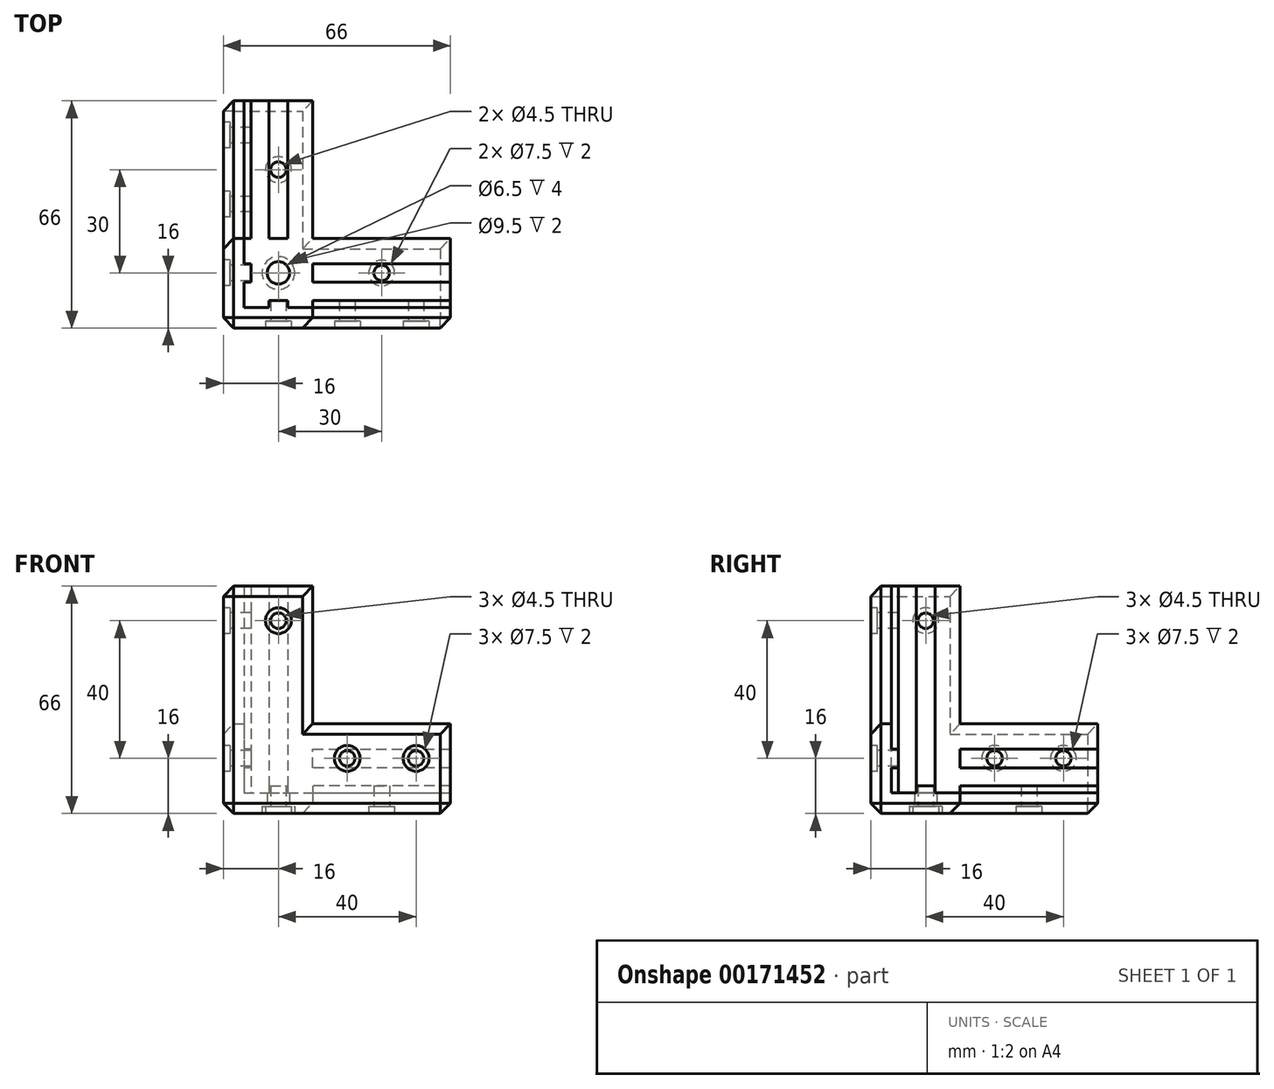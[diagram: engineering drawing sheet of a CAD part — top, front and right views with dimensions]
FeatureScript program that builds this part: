
annotation { "Feature Type Name" : "Feature", "Feature Type Description" : "" }
export const myFeature = defineFeature(function(context is Context, id is Id, definition is map)
    precondition{}
    {
        {
            var Q0;
            Q0=qCreatedBy(makeId("Top.planeOp"),FACE);
            var sketch = newSketch(context, id + "F0", { "sketchPlane" : qUnion([Q0])});
            skLineSegment(sketch, "E0", {"start": v(0, 0) * mm, "end": v(0, 66) * mm});
            skLineSegment(sketch, "E1", {"start": v(0, 66) * mm, "end": v(26, 66) * mm});
            skLineSegment(sketch, "E2", {"start": v(26, 66) * mm, "end": v(26, 26) * mm});
            skLineSegment(sketch, "E3", {"start": v(26, 26) * mm, "end": v(66, 26) * mm});
            skLineSegment(sketch, "E4", {"start": v(66, 26) * mm, "end": v(66, 0) * mm});
            skLineSegment(sketch, "E5", {"start": v(66, 0) * mm, "end": v(0, 0) * mm});
            skLineSegment(sketch, "E6", {"start": v(66, 6) * mm, "end": v(6, 6) * mm, "construction": true});
            skLineSegment(sketch, "E7", {"start": v(6, 6) * mm, "end": v(6, 66) * mm, "construction": true});
            skSolve(sketch);
        }
        {
            var Q0;
            Q0=qSketchRegion(id+"F0",true);
            extrude(context, id + "F1", {"entities" : qUnion([Q0]), "depth" : 6 * mm});
        }
        {
            var Q0;
            Q0=makeQuery(id+"F1.opExtrude","CAP_FACE",FACE,{"disambiguationData":[OSD([sQuery(id+"F0.wireOp",EDGE,"E0"),sQuery(id+"F0.wireOp",EDGE,"E1"),sQuery(id+"F0.wireOp",EDGE,"E2"),sQuery(id+"F0.wireOp",EDGE,"E3"),sQuery(id+"F0.wireOp",EDGE,"E4"),sQuery(id+"F0.wireOp",EDGE,"E5")])],"isStart":false});
            var sketch = newSketch(context, id + "F2", { "sketchPlane" : qUnion([Q0])});
            skLineSegment(sketch, "E8", {"start": v(0, 66) * mm, "end": v(6, 66) * mm});
            skLineSegment(sketch, "E9", {"start": v(6, 66) * mm, "end": v(6, 6) * mm});
            skLineSegment(sketch, "E10", {"start": v(6, 6) * mm, "end": v(66, 6) * mm});
            skLineSegment(sketch, "E11", {"start": v(66, 6) * mm, "end": v(66, 0) * mm});
            skLineSegment(sketch, "E12", {"start": v(66, 0) * mm, "end": v(0, 0) * mm});
            skLineSegment(sketch, "E13", {"start": v(0, 0) * mm, "end": v(0, 66) * mm});
            skSolve(sketch);
        }
        {
            var Q0;
            Q0=makeQuery(id+"F2.imprint","IMPRINT",FACE,{"disambiguationData":[TD([[makeQuery(id+"F2.imprint","IMPRINT",EDGE,{"derivedFrom":sQuery(id+"F2.wireOp",EDGE,"E8")}),-1.0]])]});
            extrude(context, id + "F3", {"entities" : qUnion([Q0]), "operationType" : NewBodyOperationType.ADD, "depth" : 20 * mm});
        }
        {
            var Q0;
            Q0=makeQuery(id+"F3.opExtrude","CAP_FACE",FACE,{"disambiguationData":[OSD([sQuery(id+"F2.wireOp",EDGE,"E8"),sQuery(id+"F2.wireOp",EDGE,"E9"),sQuery(id+"F2.wireOp",EDGE,"E10"),sQuery(id+"F2.wireOp",EDGE,"E11"),sQuery(id+"F2.wireOp",EDGE,"E12"),sQuery(id+"F2.wireOp",EDGE,"E13")])],"isStart":false});
            var sketch = newSketch(context, id + "F4", { "sketchPlane" : qUnion([Q0])});
            skLineSegment(sketch, "E14", {"start": v(6, 26) * mm, "end": v(0, 26) * mm});
            skLineSegment(sketch, "E15", {"start": v(0, 26) * mm, "end": v(0, 0) * mm});
            skLineSegment(sketch, "E16", {"start": v(0, 0) * mm, "end": v(26, 0) * mm});
            skLineSegment(sketch, "E17", {"start": v(26, 0) * mm, "end": v(26, 6) * mm});
            skLineSegment(sketch, "E18", {"start": v(26, 6) * mm, "end": v(6, 6) * mm});
            skLineSegment(sketch, "E19", {"start": v(6, 6) * mm, "end": v(6, 26) * mm});
            skSolve(sketch);
        }
        {
            var Q0;
            Q0=qSketchRegion(id+"F4",true);
            extrude(context, id + "F5", {"entities" : qUnion([Q0]), "operationType" : NewBodyOperationType.ADD, "depth" : 40 * mm});
        }
        {
            var Q0;
            Q0=makeQuery(id+"F1.opExtrude","CAP_FACE",FACE,{"disambiguationData":[OSD([sQuery(id+"F0.wireOp",EDGE,"E0"),sQuery(id+"F0.wireOp",EDGE,"E1"),sQuery(id+"F0.wireOp",EDGE,"E2"),sQuery(id+"F0.wireOp",EDGE,"E3"),sQuery(id+"F0.wireOp",EDGE,"E4"),sQuery(id+"F0.wireOp",EDGE,"E5")])],"isStart":false});
            var sketch = newSketch(context, id + "F6", { "sketchPlane" : qUnion([Q0])});
            skLineSegment(sketch, "E20", {"start": v(66, 16) * mm, "end": v(6, 16) * mm, "construction": true});
            skLineSegment(sketch, "E21", {"start": v(16, 66) * mm, "end": v(16, 6) * mm, "construction": true});
            skLineSegment(sketch, "E22", {"start": v(16, 6) * mm, "end": v(18.71, 6) * mm});
            skLineSegment(sketch, "E23", {"start": v(18.71, 6) * mm, "end": v(18.71, 8) * mm});
            skLineSegment(sketch, "E24", {"start": v(18.71, 8) * mm, "end": v(13.3, 8) * mm});
            skLineSegment(sketch, "E25", {"start": v(13.3, 8) * mm, "end": v(13.3, 6) * mm});
            skLineSegment(sketch, "E26", {"start": v(13.3, 6) * mm, "end": v(16, 6) * mm});
            skLineSegment(sketch, "E27", {"start": v(6, 16) * mm, "end": v(6, 18.7) * mm});
            skLineSegment(sketch, "E28", {"start": v(6, 18.7) * mm, "end": v(8, 18.7) * mm});
            skLineSegment(sketch, "E29", {"start": v(8, 18.7) * mm, "end": v(8, 13.29) * mm});
            skLineSegment(sketch, "E30", {"start": v(8, 13.29) * mm, "end": v(6, 13.29) * mm});
            skLineSegment(sketch, "E31", {"start": v(6, 13.29) * mm, "end": v(6, 16) * mm});
            skSolve(sketch);
        }
        {
            var Q0;
            Q0=qSketchRegion(id+"F6",true);
            extrude(context, id + "F7", {"entities" : qUnion([Q0]), "operationType" : NewBodyOperationType.ADD, "depth" : 60 * mm});
        }
        {
            var Q0;
            Q0=makeQuery(id+"F1.opExtrude","CAP_FACE",FACE,{"disambiguationData":[OSD([sQuery(id+"F0.wireOp",EDGE,"E0"),sQuery(id+"F0.wireOp",EDGE,"E1"),sQuery(id+"F0.wireOp",EDGE,"E2"),sQuery(id+"F0.wireOp",EDGE,"E3"),sQuery(id+"F0.wireOp",EDGE,"E4"),sQuery(id+"F0.wireOp",EDGE,"E5")])],"isStart":false});
            var sketch = newSketch(context, id + "F8", { "sketchPlane" : qUnion([Q0])});
            skLineSegment(sketch, "E32", {"start": v(66, 16) * mm, "end": v(8, 16) * mm, "construction": true});
            skLineSegment(sketch, "E33", {"start": v(66, 16) * mm, "end": v(66, 18.7) * mm});
            skLineSegment(sketch, "E34", {"start": v(66, 18.7) * mm, "end": v(26, 18.7) * mm});
            skLineSegment(sketch, "E35", {"start": v(26, 18.7) * mm, "end": v(26, 13.29) * mm});
            skLineSegment(sketch, "E36", {"start": v(26, 13.29) * mm, "end": v(66, 13.29) * mm});
            skLineSegment(sketch, "E37", {"start": v(66, 13.29) * mm, "end": v(66, 16) * mm});
            skLineSegment(sketch, "E38", {"start": v(16, 66) * mm, "end": v(16, 8) * mm, "construction": true});
            skLineSegment(sketch, "E39", {"start": v(16, 66) * mm, "end": v(13.3, 66) * mm});
            skLineSegment(sketch, "E40", {"start": v(13.3, 66) * mm, "end": v(13.3, 26) * mm});
            skLineSegment(sketch, "E41", {"start": v(13.3, 26) * mm, "end": v(18.7, 26) * mm});
            skLineSegment(sketch, "E42", {"start": v(18.7, 26) * mm, "end": v(18.7, 66) * mm});
            skLineSegment(sketch, "E43", {"start": v(18.7, 66) * mm, "end": v(16, 66) * mm});
            skSolve(sketch);
        }
        {
            var Q0;
            Q0=qSketchRegion(id+"F8",true);
            extrude(context, id + "F9", {"entities" : qUnion([Q0]), "operationType" : NewBodyOperationType.ADD, "depth" : 2 * mm});
        }
        {
            var Q0;
            {var subQ1=sQuery(id+"F2.wireOp",EDGE,"E10");var subQ2=sQuery(id+"F0.wireOp",EDGE,"E4");var subQ3=sQuery(id+"F4.wireOp",EDGE,"E18");Q0=makeQuery(id+"F7.boolean.opBoolean","SPLIT",FACE,{"disambiguationData":[TD([makeQuery(id+"F1.opExtrude","SWEPT_FACE",FACE,{"disambiguationData":[OSD([subQ2])]})])],"derivedFrom":makeQuery(id+"F5.boolean.opBoolean","MERGE",FACE,{"derivedFrom":[makeQuery(id+"F3.opExtrude","SWEPT_FACE",FACE,{"disambiguationData":[OSD([subQ1])]}),makeQuery(id+"F5.opExtrude","SWEPT_FACE",FACE,{"disambiguationData":[OSD([subQ3])]})]})});}
            var sketch = newSketch(context, id + "F10", { "sketchPlane" : qUnion([Q0])});
            skLineSegment(sketch, "E44", {"start": v(-66, 16) * mm, "end": v(-26, 16) * mm, "construction": true});
            skLineSegment(sketch, "E45", {"start": v(-66, 16) * mm, "end": v(-66, 13.3) * mm});
            skLineSegment(sketch, "E46", {"start": v(-66, 13.3) * mm, "end": v(-26, 13.3) * mm});
            skLineSegment(sketch, "E47", {"start": v(-26, 13.3) * mm, "end": v(-26, 16) * mm});
            skLineSegment(sketch, "E48", {"start": v(-26, 18.71) * mm, "end": v(-66, 18.71) * mm});
            skLineSegment(sketch, "E49", {"start": v(-66, 18.71) * mm, "end": v(-66, 16) * mm});
            skLineSegment(sketch, "E50", {"start": v(-26, 18.71) * mm, "end": v(-26, 16) * mm});
            skSolve(sketch);
        }
        {
            var Q0;
            Q0=qSketchRegion(id+"F10",true);
            extrude(context, id + "F11", {"entities" : qUnion([Q0]), "operationType" : NewBodyOperationType.ADD, "depth" : 2 * mm});
        }
        {
            var Q0;
            {var subQ0=sQuery(id+"F2.wireOp",EDGE,"E9");var subQ3=sQuery(id+"F0.wireOp",EDGE,"E1");var subQ5=sQuery(id+"F4.wireOp",EDGE,"E19");Q0=makeQuery(id+"F7.boolean.opBoolean","SPLIT",FACE,{"disambiguationData":[TD([makeQuery(id+"F1.opExtrude","SWEPT_FACE",FACE,{"disambiguationData":[OSD([subQ3])]})])],"derivedFrom":makeQuery(id+"F5.boolean.opBoolean","MERGE",FACE,{"derivedFrom":[makeQuery(id+"F3.opExtrude","SWEPT_FACE",FACE,{"disambiguationData":[OSD([subQ0])]}),makeQuery(id+"F5.opExtrude","SWEPT_FACE",FACE,{"disambiguationData":[OSD([subQ5])]})]})});}
            var sketch = newSketch(context, id + "F12", { "sketchPlane" : qUnion([Q0])});
            skLineSegment(sketch, "E51", {"start": v(66, 16) * mm, "end": v(26, 16) * mm, "construction": true});
            skLineSegment(sketch, "E52", {"start": v(66, 16) * mm, "end": v(66, 18.71) * mm});
            skLineSegment(sketch, "E53", {"start": v(66, 18.71) * mm, "end": v(26, 18.7) * mm});
            skLineSegment(sketch, "E54", {"start": v(26, 18.7) * mm, "end": v(26, 13.29) * mm});
            skLineSegment(sketch, "E55", {"start": v(26, 13.29) * mm, "end": v(66, 13.29) * mm});
            skLineSegment(sketch, "E56", {"start": v(66, 16) * mm, "end": v(66, 13.29) * mm});
            skSolve(sketch);
        }
        {
            var Q0;
            Q0=qSketchRegion(id+"F12",true);
            extrude(context, id + "F13", {"entities" : qUnion([Q0]), "operationType" : NewBodyOperationType.ADD, "depth" : 2 * mm});
        }
        {
            var Q0;
            Q0=makeQuery(id+"F5.boolean.opBoolean","MERGE",FACE,{"derivedFrom":[makeQuery(id+"F3.boolean.opBoolean","MERGE",FACE,{"derivedFrom":[makeQuery(id+"F1.opExtrude","SWEPT_FACE",FACE,{"disambiguationData":[OSD([sQuery(id+"F0.wireOp",EDGE,"E5")])]}),makeQuery(id+"F3.opExtrude","SWEPT_FACE",FACE,{"disambiguationData":[OSD([sQuery(id+"F2.wireOp",EDGE,"E12")])]})]}),makeQuery(id+"F5.opExtrude","SWEPT_FACE",FACE,{"disambiguationData":[OSD([sQuery(id+"F4.wireOp",EDGE,"E16")])]})]});
            var sketch = newSketch(context, id + "F14", { "sketchPlane" : qUnion([Q0])});
            skLineSegment(sketch, "E57", {"start": v(6, 66) * mm, "end": v(6, 6) * mm, "construction": true});
            skLineSegment(sketch, "E58", {"start": v(6, 6) * mm, "end": v(66, 6) * mm, "construction": true});
            skCircle(sketch, "E59", {"center": v(56, 16) * mm, "radius": 2.25 * mm});
            skCircle(sketch, "E60", {"center": v(36, 16) * mm, "radius": 2.25 * mm});
            skCircle(sketch, "E61", {"center": v(16, 56) * mm, "radius": 2.25 * mm});
            skLineSegment(sketch, "E62", {"start": v(26, 26) * mm, "end": v(6, 26) * mm, "construction": true});
            skLineSegment(sketch, "E63", {"start": v(26, 26) * mm, "end": v(26, 6) * mm, "construction": true});
            skSolve(sketch);
        }
        {
            var Q0;
            Q0=makeQuery(id+"F14.imprint","IMPRINT",FACE,{"disambiguationData":[TD([[makeQuery(id+"F14.imprint","IMPRINT",EDGE,{"derivedFrom":sQuery(id+"F14.wireOp",EDGE,"E59")}),1.0]])]});
            var Q1;
            Q1=makeQuery(id+"F14.imprint","IMPRINT",FACE,{"disambiguationData":[TD([[makeQuery(id+"F14.imprint","IMPRINT",EDGE,{"derivedFrom":sQuery(id+"F14.wireOp",EDGE,"E61")}),1.0]])]});
            var Q2;
            Q2=makeQuery(id+"F14.imprint","IMPRINT",FACE,{"disambiguationData":[TD([[makeQuery(id+"F14.imprint","IMPRINT",EDGE,{"derivedFrom":sQuery(id+"F14.wireOp",EDGE,"E60")}),1.0]])]});
            extrude(context, id + "F15", {"entities" : qUnion([Q0, Q1, Q2]), "operationType" : NewBodyOperationType.REMOVE, "endBound" : BoundingType.UP_TO_NEXT, "oppositeDirection" : true, "depth" : 25 * mm});
        }
        {
            var Q0;
            Q0=makeQuery(id+"F5.boolean.opBoolean","MERGE",FACE,{"derivedFrom":[makeQuery(id+"F3.boolean.opBoolean","MERGE",FACE,{"derivedFrom":[makeQuery(id+"F1.opExtrude","SWEPT_FACE",FACE,{"disambiguationData":[OSD([sQuery(id+"F0.wireOp",EDGE,"E0")])]}),makeQuery(id+"F3.opExtrude","SWEPT_FACE",FACE,{"disambiguationData":[OSD([sQuery(id+"F2.wireOp",EDGE,"E13")])]})]}),makeQuery(id+"F5.opExtrude","SWEPT_FACE",FACE,{"disambiguationData":[OSD([sQuery(id+"F4.wireOp",EDGE,"E15")])]})]});
            var sketch = newSketch(context, id + "F16", { "sketchPlane" : qUnion([Q0])});
            skLineSegment(sketch, "E64", {"start": v(-6, 66) * mm, "end": v(-6, 6) * mm, "construction": true});
            skLineSegment(sketch, "E65", {"start": v(-6, 6) * mm, "end": v(-66, 6) * mm, "construction": true});
            skCircle(sketch, "E66", {"center": v(-16, 56) * mm, "radius": 2.25 * mm});
            skCircle(sketch, "E67", {"center": v(-56, 16) * mm, "radius": 2.25 * mm});
            skCircle(sketch, "E68", {"center": v(-36, 16) * mm, "radius": 2.25 * mm});
            skSolve(sketch);
        }
        {
            var Q0;
            Q0=qSketchRegion(id+"F16",true);
            extrude(context, id + "F17", {"entities" : qUnion([Q0]), "operationType" : NewBodyOperationType.REMOVE, "endBound" : BoundingType.UP_TO_NEXT, "oppositeDirection" : true, "depth" : 25 * mm});
        }
        {
            var Q0;
            Q0=makeQuery(id+"F1.opExtrude","CAP_FACE",FACE,{"disambiguationData":[OSD([sQuery(id+"F0.wireOp",EDGE,"E0"),sQuery(id+"F0.wireOp",EDGE,"E1"),sQuery(id+"F0.wireOp",EDGE,"E2"),sQuery(id+"F0.wireOp",EDGE,"E3"),sQuery(id+"F0.wireOp",EDGE,"E4"),sQuery(id+"F0.wireOp",EDGE,"E5")])],"isStart":true});
            var sketch = newSketch(context, id + "F18", { "sketchPlane" : qUnion([Q0])});
            skLineSegment(sketch, "E69", {"start": v(66, -6) * mm, "end": v(6, -6) * mm, "construction": true});
            skLineSegment(sketch, "E70", {"start": v(6, -6) * mm, "end": v(6, -66) * mm, "construction": true});
            skCircle(sketch, "E71", {"center": v(16, -16) * mm, "radius": 3.25 * mm});
            skCircle(sketch, "E72", {"center": v(46, -16) * mm, "radius": 2.25 * mm});
            skCircle(sketch, "E73", {"center": v(16, -46) * mm, "radius": 2.25 * mm});
            skSolve(sketch);
        }
        {
            var Q0;
            Q0=qSketchRegion(id+"F18",true);
            extrude(context, id + "F19", {"entities" : qUnion([Q0]), "operationType" : NewBodyOperationType.REMOVE, "endBound" : BoundingType.UP_TO_NEXT, "oppositeDirection" : true, "depth" : 25 * mm});
        }
        {
            var Q0;
            Q0=makeQuery(id+"F5.boolean.opBoolean","MERGE",FACE,{"derivedFrom":[makeQuery(id+"F3.boolean.opBoolean","MERGE",FACE,{"derivedFrom":[makeQuery(id+"F1.opExtrude","SWEPT_FACE",FACE,{"disambiguationData":[OSD([sQuery(id+"F0.wireOp",EDGE,"E5")])]}),makeQuery(id+"F3.opExtrude","SWEPT_FACE",FACE,{"disambiguationData":[OSD([sQuery(id+"F2.wireOp",EDGE,"E12")])]})]}),makeQuery(id+"F5.opExtrude","SWEPT_FACE",FACE,{"disambiguationData":[OSD([sQuery(id+"F4.wireOp",EDGE,"E16")])]})]});
            var sketch = newSketch(context, id + "F20", { "sketchPlane" : qUnion([Q0])});
            skCircle(sketch, "E74", {"center": v(16, 56) * mm, "radius": 3.75 * mm});
            skCircle(sketch, "E75", {"center": v(36, 16) * mm, "radius": 3.75 * mm});
            skCircle(sketch, "E76", {"center": v(56, 16) * mm, "radius": 3.75 * mm});
            skSolve(sketch);
        }
        {
            var Q0;
            Q0=qSketchRegion(id+"F20",true);
            extrude(context, id + "F21", {"entities" : qUnion([Q0]), "operationType" : NewBodyOperationType.REMOVE, "oppositeDirection" : true, "depth" : 2 * mm});
        }
        {
            var Q0;
            Q0=makeQuery(id+"F5.boolean.opBoolean","MERGE",FACE,{"derivedFrom":[makeQuery(id+"F3.boolean.opBoolean","MERGE",FACE,{"derivedFrom":[makeQuery(id+"F1.opExtrude","SWEPT_FACE",FACE,{"disambiguationData":[OSD([sQuery(id+"F0.wireOp",EDGE,"E0")])]}),makeQuery(id+"F3.opExtrude","SWEPT_FACE",FACE,{"disambiguationData":[OSD([sQuery(id+"F2.wireOp",EDGE,"E13")])]})]}),makeQuery(id+"F5.opExtrude","SWEPT_FACE",FACE,{"disambiguationData":[OSD([sQuery(id+"F4.wireOp",EDGE,"E15")])]})]});
            var sketch = newSketch(context, id + "F22", { "sketchPlane" : qUnion([Q0])});
            skCircle(sketch, "E77", {"center": v(-16, 56) * mm, "radius": 3.75 * mm});
            skCircle(sketch, "E78", {"center": v(-36, 16) * mm, "radius": 3.75 * mm});
            skCircle(sketch, "E79", {"center": v(-56, 16) * mm, "radius": 3.75 * mm});
            skSolve(sketch);
        }
        {
            var Q0;
            Q0=qSketchRegion(id+"F22",true);
            extrude(context, id + "F23", {"entities" : qUnion([Q0]), "operationType" : NewBodyOperationType.REMOVE, "oppositeDirection" : true, "depth" : 2 * mm});
        }
        {
            var Q0;
            Q0=makeQuery(id+"F1.opExtrude","CAP_FACE",FACE,{"disambiguationData":[OSD([sQuery(id+"F0.wireOp",EDGE,"E0"),sQuery(id+"F0.wireOp",EDGE,"E1"),sQuery(id+"F0.wireOp",EDGE,"E2"),sQuery(id+"F0.wireOp",EDGE,"E3"),sQuery(id+"F0.wireOp",EDGE,"E4"),sQuery(id+"F0.wireOp",EDGE,"E5")])],"isStart":true});
            var sketch = newSketch(context, id + "F24", { "sketchPlane" : qUnion([Q0])});
            skCircle(sketch, "E80", {"center": v(16, -46) * mm, "radius": 3.75 * mm});
            skCircle(sketch, "E81", {"center": v(16, -16) * mm, "radius": 4.75 * mm});
            skCircle(sketch, "E82", {"center": v(46, -16) * mm, "radius": 3.75 * mm});
            skSolve(sketch);
        }
        {
            var Q0;
            Q0=qSketchRegion(id+"F24",true);
            extrude(context, id + "F25", {"entities" : qUnion([Q0]), "operationType" : NewBodyOperationType.REMOVE, "oppositeDirection" : true, "depth" : 2 * mm});
        }
        {
            var Q0;
            Q0=makeQuery(id+"F1.opExtrude","CAP_EDGE",EDGE,{"disambiguationData":[OSD([sQuery(id+"F0.wireOp",EDGE,"E5")])],"isStart":true});
            var Q1;
            Q1=makeQuery(id+"F1.opExtrude","CAP_EDGE",EDGE,{"disambiguationData":[OSD([sQuery(id+"F0.wireOp",EDGE,"E0")])],"isStart":true});
            var Q2;
            Q2=makeQuery(id+"F5.boolean.opBoolean","MERGE",EDGE,{"derivedFrom":[makeQuery(id+"F3.boolean.opBoolean","MERGE",EDGE,{"derivedFrom":[makeQuery(id+"F1.opExtrude","SWEPT_EDGE",EDGE,{"disambiguationData":[OSD([sQuery(id+"F0.wireOp",EDGE,"E0"),sQuery(id+"F0.wireOp",EDGE,"E5")])]}),makeQuery(id+"F3.opExtrude","SWEPT_EDGE",EDGE,{"disambiguationData":[OSD([sQuery(id+"F2.wireOp",EDGE,"E12"),sQuery(id+"F2.wireOp",EDGE,"E13")])]})]}),makeQuery(id+"F5.opExtrude","SWEPT_EDGE",EDGE,{"disambiguationData":[OSD([sQuery(id+"F4.wireOp",EDGE,"E15"),sQuery(id+"F4.wireOp",EDGE,"E16")])]})]});
            var Q3;
            Q3=makeQuery(id+"F5.opExtrude","SWEPT_EDGE",EDGE,{"disambiguationData":[OSD([sQuery(id+"F2.wireOp",EDGE,"E13"),sQuery(id+"F4.wireOp",EDGE,"E14"),sQuery(id+"F4.wireOp",EDGE,"E15")])]});
            var Q4;
            Q4=makeQuery(id+"F3.opExtrude","CAP_EDGE",EDGE,{"disambiguationData":[OSD([sQuery(id+"F2.wireOp",EDGE,"E13")])],"isStart":false});
            var Q5;
            Q5=makeQuery(id+"F5.opExtrude","SWEPT_EDGE",EDGE,{"disambiguationData":[OSD([sQuery(id+"F2.wireOp",EDGE,"E12"),sQuery(id+"F4.wireOp",EDGE,"E16"),sQuery(id+"F4.wireOp",EDGE,"E17")])]});
            var Q6;
            Q6=makeQuery(id+"F3.opExtrude","CAP_EDGE",EDGE,{"disambiguationData":[OSD([sQuery(id+"F2.wireOp",EDGE,"E12")])],"isStart":false});
            var Q7;
            Q7=makeQuery(id+"F5.opExtrude","CAP_EDGE",EDGE,{"disambiguationData":[OSD([sQuery(id+"F4.wireOp",EDGE,"E15")])],"isStart":false});
            var Q8;
            Q8=makeQuery(id+"F5.opExtrude","CAP_EDGE",EDGE,{"disambiguationData":[OSD([sQuery(id+"F4.wireOp",EDGE,"E16")])],"isStart":false});
            var Q9;
            Q9=makeQuery(id+"F3.boolean.opBoolean","MERGE",EDGE,{"derivedFrom":[makeQuery(id+"F1.opExtrude","SWEPT_EDGE",EDGE,{"disambiguationData":[OSD([sQuery(id+"F0.wireOp",EDGE,"E0"),sQuery(id+"F0.wireOp",EDGE,"E1")])]}),makeQuery(id+"F3.opExtrude","SWEPT_EDGE",EDGE,{"disambiguationData":[OSD([sQuery(id+"F2.wireOp",EDGE,"E8"),sQuery(id+"F2.wireOp",EDGE,"E13")])]})]});
            var Q10;
            Q10=makeQuery(id+"F1.opExtrude","CAP_EDGE",EDGE,{"disambiguationData":[OSD([sQuery(id+"F0.wireOp",EDGE,"E1")])],"isStart":true});
            var Q11;
            Q11=makeQuery(id+"F3.boolean.opBoolean","MERGE",EDGE,{"derivedFrom":[makeQuery(id+"F1.opExtrude","SWEPT_EDGE",EDGE,{"disambiguationData":[OSD([sQuery(id+"F0.wireOp",EDGE,"E4"),sQuery(id+"F0.wireOp",EDGE,"E5")])]}),makeQuery(id+"F3.opExtrude","SWEPT_EDGE",EDGE,{"disambiguationData":[OSD([sQuery(id+"F2.wireOp",EDGE,"E11"),sQuery(id+"F2.wireOp",EDGE,"E12")])]})]});
            var Q12;
            Q12=makeQuery(id+"F1.opExtrude","CAP_EDGE",EDGE,{"disambiguationData":[OSD([sQuery(id+"F0.wireOp",EDGE,"E4")])],"isStart":true});
            var Q13;
            Q13=makeQuery(id+"F1.opExtrude","CAP_EDGE",EDGE,{"disambiguationData":[OSD([sQuery(id+"F0.wireOp",EDGE,"E3")])],"isStart":true});
            var Q14;
            Q14=makeQuery(id+"F1.opExtrude","CAP_EDGE",EDGE,{"disambiguationData":[OSD([sQuery(id+"F0.wireOp",EDGE,"E2")])],"isStart":true});
            chamfer(context, id + "F26", {"entities" : qUnion([Q0, Q1, Q2, Q3, Q4, Q5, Q6, Q7, Q8, Q9, Q10, Q11, Q12, Q13, Q14]), "width" : 3 * mm, "tangentPropagation" : true});
        }
    });
